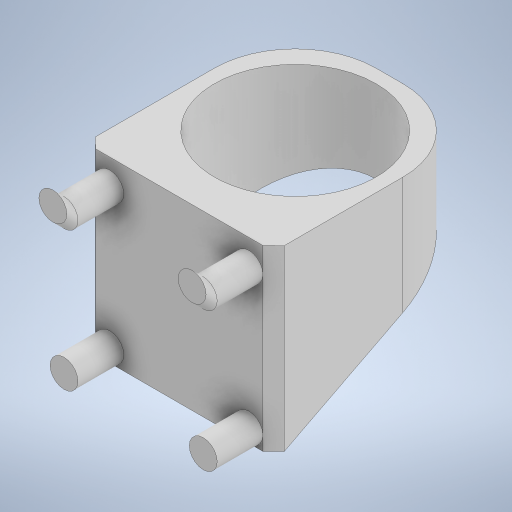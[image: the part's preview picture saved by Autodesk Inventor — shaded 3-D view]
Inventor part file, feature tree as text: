
AUTODESK INVENTOR PART (.ipt)
format: ipt  version: 2024 (Build 280153000, 153)  size: 345,600 bytes
history: native  units: mm
features: chamfer x5, sketch x5, other x4, extrude x4, pattern_linear x3, fillet x2, loft x1
ambient origin geometry x8: Origin, YZ Plane, XZ Plane, XY Plane, X Axis, Y Axis, Z Axis, Center Point
bodies: Body1 (feature_tree)
feature tree (24):
  other  "Твердое тело1"
  extrude  "Выдавливание1"  Depth=1.85mm TaperAngle=0.0deg
  extrude  "Выдавливание2"  Depth=29.95mm
  pattern_linear  "Прямоуг.массив1"  Spacing1=31.95mm  [1 undecoded]
  extrude  "Выдавливание3"  Depth=5.0mm
  extrude  "Выдавливание4"  Depth=8.2mm TaperAngle=0.0deg
  fillet  "Сопряжение1"  Radius=20.0mm
  pattern_linear  "Прямоуг.массив2"  Spacing1=24.95mm  [1 undecoded]
  fillet  "Сопряжение2"  Radius=15.0mm
  other  "РабПлоскость1"
  loft  "Лофт1"
  pattern_linear  "Прямоуг.массив3"  Spacing1=29.0mm  [1 undecoded]
  chamfer  "Фаска5"  Distance=15.0mm
  chamfer  "Фаска3"  [1 undecoded]
  chamfer  "Фаска4"  Distance=29.0mm
  other  "Удаление грани1"
  chamfer  "Фаска1"  Distance=14.5mm
  chamfer  "Фаска2"  Distance=10.0mm
  sketch  "Эскиз1"
  sketch  "Эскиз2"
  sketch  "Эскиз3"
  sketch  "Эскиз4"
  sketch  "Эскиз7"
  other  "Ребра1"
note: 4 required parameter values undecoded (feature->parameter linkage not recoverable at this tier; creation-order binding heuristic only, values carry confidence <= 0.55)
